# Revit family: lucio_-_lud_500_840_d_00810809_77ad
name_source: partatom
category: Lighting Fixtures
units: mm (PartAtom-declared; Revit-internal decimal feet)

## family parameters
Cut with Voids When Loaded = No
Host = Face
Light Source = No
Part Type = Normal
Room Calculation Point = No
Round Connector Dimension = Use Diameter
Shared = No

## types (1)
- LUCIO - LUD 500/840/D (1 x LED, 300 lm, 4000K)
    Apparent Load = 4 VA
    Approval mark = CE
    CIE Flux Codes = 84 97 99 100 100
    Color Rendering = 80-89
    Color Temperature = 4000K
    Control Gear = Electronic ballast
    Default Elevation = 1800 mm
    Description = LUD 500/840/D|Task luminaire|light source: LED module|work equipment: Electronic plug-in transformer|connected load: 100-240 V, 50/60 Hz|Power consumption: approx. 4 W|standby: approx. 0,30|power factor: approx. 0,970|luminous flux: 300 lm|luminous efficacy: 75 lm/W|Illuminance efficiency factor: 0 lx/W|colour temperature: Cold white, ca. 4000 K|color rendering index (CRI): >= 80|chromaticity tolerance:  3 SDCM|class of protection: II with plug-in power supply, III without plug-in power supply|technology: Continuously dimmable|luminaire body|material: Plastic|surface: Untreated|colour: Umbra grey|lamp cover: Polycarbonate (PC), Satine|tubular sections|material: Tubular aluminium section|surface: Anodized|Form: Tubular section upright|colour: Titanium|weight (net): approx. 1.9 kg|mains lead: 1.50 m Mains plug CEE 7/XVI|Fastening: Adaptor (accessory), Table base, Table clamp (accessory)|glare control: Optics|special features: Push button in luminaire head|Approval mark: VDE - ENEC|
    Frequency = 50 Hz
    Height = 55 mm
    Lamp = 1 x LED
    Lamp Light Flux = 300 lm
    Lamp count = 1
    Length = 90 mm
    Luminous efficacy = 75 lm/W
    Manufacturer = Waldmann
    ModVariant = No
    Model = 00810809
    Mounting Place = Table
    Mounting Type = Surface mounted
    Number of Poles = 1
    OnlyDefault = Yes
    Power Factor = 1
    Product Name = LUCIO - LUD 500/840/D
    Product group = Task luminaire (office)
    ProductGroupID = 21
    Protection Class = Protection class II
    Protection Degree = IP 20
    RLX_Detail_Level = 1
    RLX_Emergency_Light_Flux = 0 lm
    RLX_Emergency_Type = 0
    RLX_Emergency_Type_DB = No
    RlxData = <blob elided: 84961 chars, md5=9a1de5fb>
    Socket = socket
    Standby Power = 0 W
    System Light Flux = 300 lm
    System Power = 4 W
    Type Comments = Product without accessories
    Type Image = 00810809.jpg
    URL = http://relux.com
    VarID = ---
    Voltage = 230 V
    Voltage Range = 220-240 V
    Weight = 0.00 kg
    Width = 0 mm  [stored 0 ft]

note: [stored X ft] marks values corroborated as IEEE doubles in the binary element streams (Revit-internal decimal feet)

## geometry (parser evidence)
native form markers: Sweep x13
no freeform markers — native parametric forms only
